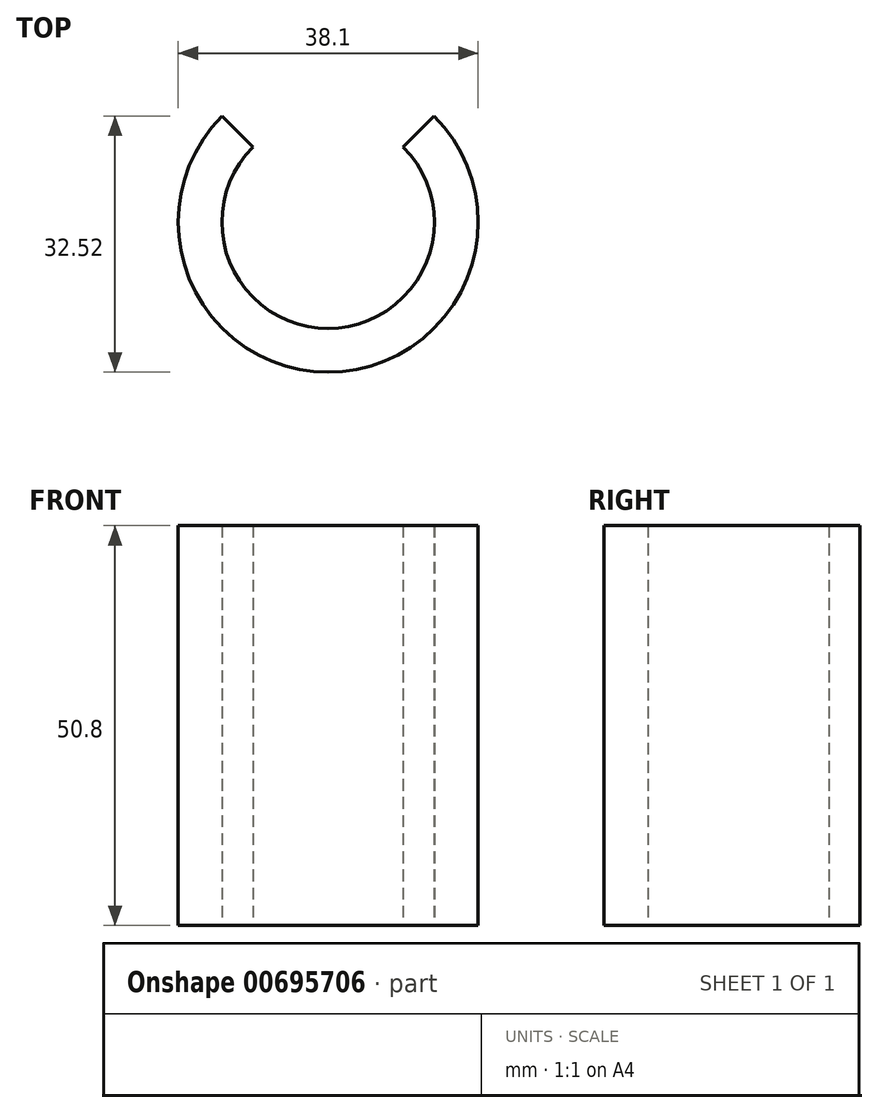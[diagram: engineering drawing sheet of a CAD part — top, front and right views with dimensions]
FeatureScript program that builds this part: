
annotation { "Feature Type Name" : "Feature", "Feature Type Description" : "" }
export const myFeature = defineFeature(function(context is Context, id is Id, definition is map)
    precondition{}
    {
        {
            var Q0;
            Q0=qCreatedBy(makeId("Top.planeOp"),FACE);
            var sketch = newSketch(context, id + "F0", { "sketchPlane" : qUnion([Q0])});
            skCircle(sketch, "E0", {"center": v(0, 0) * mm, "radius": 13.5 * mm});
            skArc(sketch, "E1", {"start": v(-13.47, 13.47) * mm, "mid": v(0, -19.05) * mm, "end": v(13.47, 13.47) * mm});
            skLineSegment(sketch, "E2", {"start": v(0, 0) * mm, "end": v(0, 19.05) * mm});
            skLineSegment(sketch, "E3", {"start": v(0, 0) * mm, "end": v(13.47, 13.47) * mm});
            skLineSegment(sketch, "E4.MirrorCS", {"start": v(0, 0) * mm, "end": v(-13.47, 13.47) * mm});
            skSolve(sketch);
        }
        {
            var Q0;
            {var subQ5=sQuery(id+"F0.wireOp",EDGE,"E1");Q0=makeQuery(id+"F0.imprint","IMPRINT",FACE,{"disambiguationData":[TD([[makeQuery(id+"F0.imprint","IMPRINT",EDGE,{"derivedFrom":subQ5}),1.0]])]});}
            extrude(context, id + "F1", {"entities" : qUnion([Q0]), "depth" : 50.8 * mm, "offsetDistance" : 25.4 * mm});
        }
    });
